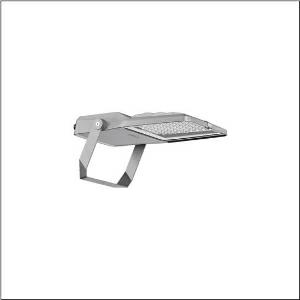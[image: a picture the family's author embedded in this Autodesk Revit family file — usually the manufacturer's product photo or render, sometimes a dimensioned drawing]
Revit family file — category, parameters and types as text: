
# Revit family: floodlight_fl_21_mini___pl64_5xa7776d4e1a_c051
name_source: partatom
category: Lighting Fixtures
units: mm (PartAtom-declared; Revit-internal decimal feet)

## family parameters
Cut with Voids When Loaded = No
Host = Face
Light Source = No
Part Type = Normal
Room Calculation Point = No
Round Connector Dimension = Use Diameter
Shared = No

## types (1)
- --- (1 x LED, 17960 lm, 142.9 W, 4000K)
    Apparent Load = 143 VA
    CIE Flux Codes = 28 80 98 100 100
    Color Rendering = 70
    Color Temperature = 4000K
    Default Elevation = 1800 mm
    Description = Floodlight FL 21 mini, floodlight, primary light control with lens, of PMMA, primary optical cover: protective disc, of toughened safety glass, transparent, light distribution: PL64, light emission: direct distribution, installation type: surface-mounted, LED, High Power LED, rated luminous flux: 17.960lm, luminous efficacy: 126lm/W, light colour: 740, colour temperature: 4000K, control gear: D4iSmart Interface (Zhaga), control: overheat protection, constant luminous flux control, time-dependent luminous flux control, flexible luminous flux parameterisation, pre-setting: logarithmic dimming characteristic, with terminal, 6-pole, mains connection: 220..240V, AC, 50/60Hz, start of lifetime: 143W, end of service life: 151W, reduction: 63W, mounting bracket, of diecast aluminium, powder-coated, Siteco® metallic grey (DB 702S), corrosivity category C5 mid according to DIN EN ISO 12944, suitable for swimming pools, chlorine-resistant, sealing non-destructively replaceable, mounting bracket, of steel, galvanised, powder-coated, Siteco® metallic grey (DB 702S), Smart Interface below and above, protection rating (complete): IP66, insulation class (complete): insulation class II (safety insulation), certification: CE, ENEC, VDE, protection symbol: D, impact resistance: IK08, permissible operating ambient temperature: -40..+40°C, permissible operating ambient temperature for outdoor applications: -40..+50°C, standard: DIN EN 12944, LABS conformity tested according to VDMA 24364:2018-05, packaging unit: 1 piece

Light Distribution: PL64
    Height = 70 mm
    Lamp = 1 x LED
    Lamp Light Flux = 17960 lm
    Lamp Power = 142.9 W
    Lamp count = 1
    Length = 485 mm
    Luminous efficacy = 126 lm/W
    Manufacturer = Siteco
    ModVariant = No
    Model = 5XA7776D4E1A
    Number of Poles = 1
    OnlyDefault = Yes
    Power Factor = 1
    Product Name = Floodlight FL 21 mini | PL64
    Product group = floodlight | pylon annexe
    ProductGroupID = 6200
    Protection Class = Protection class II
    Protection Degree = IP 66
    RLX_Detail_Level = 1
    RLX_Emergency_Light_Flux = 0 lm
    RLX_Emergency_Type = 0
    RLX_Emergency_Type_DB = No
    RlxData = <blob elided: 96245 chars, md5=f92dfd89>
    Socket = socket
    Standby Power = 0 W
    System Light Flux = 17960 lm
    System Power = 143 W
    Type Comments = factory setting: luminous flux: 100 % | dim-lin: 254 | 730 mA
    Type Image = l_1006845.jpg
    URL = http://relux.com
    VarID = @adj_097052
    Voltage = 0 V
    Weight = 0.00 kg
    Width = 337 mm

## geometry (parser evidence)
native form markers: Blend x4, Sweep x14
no freeform markers — native parametric forms only
